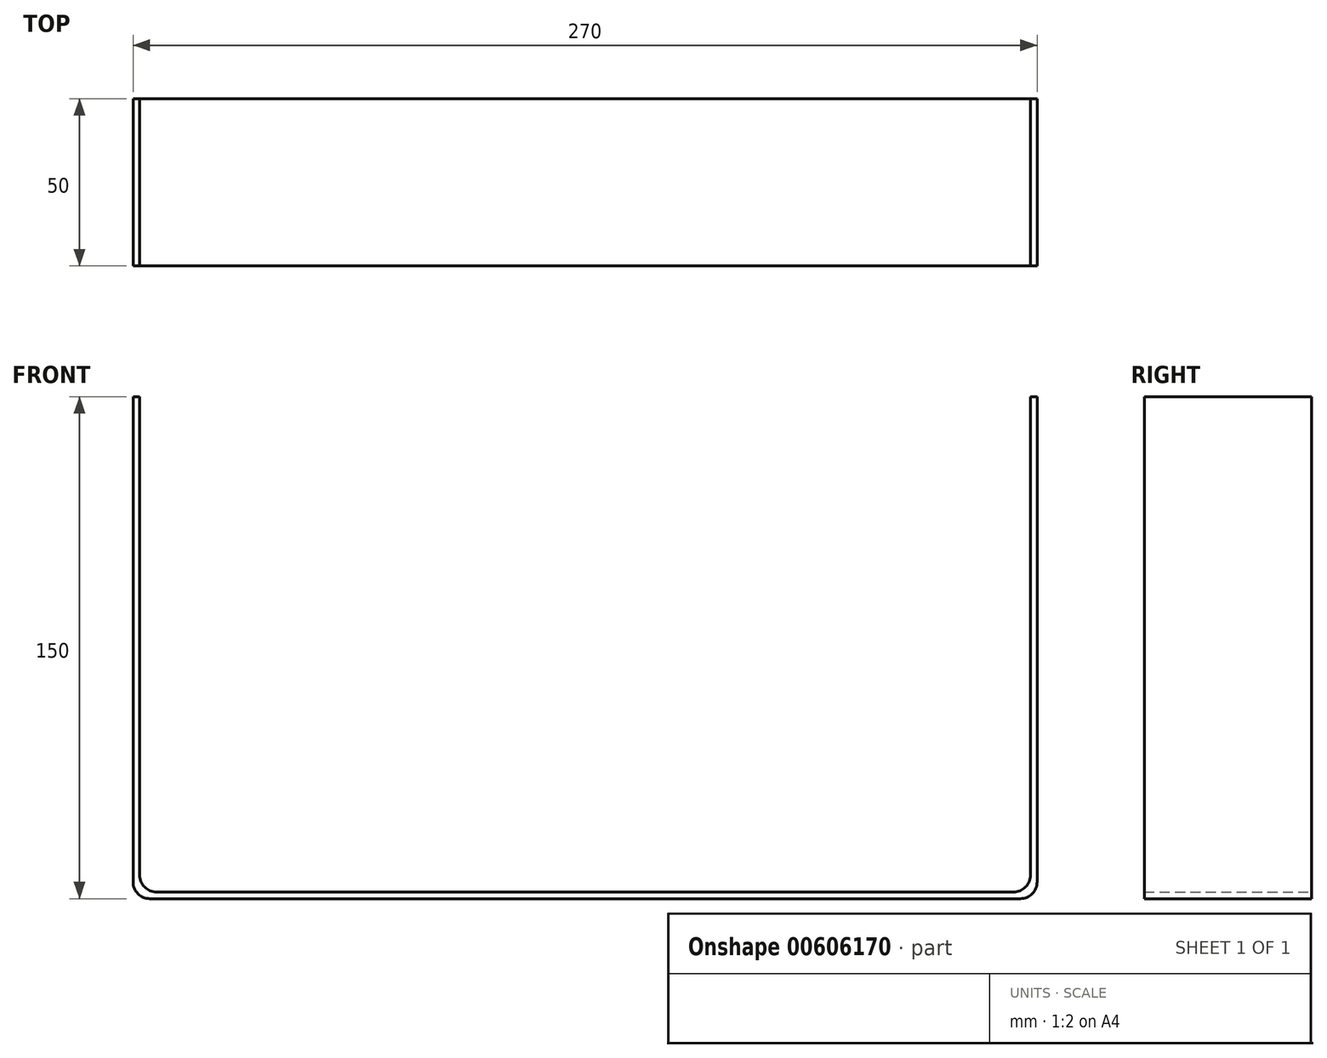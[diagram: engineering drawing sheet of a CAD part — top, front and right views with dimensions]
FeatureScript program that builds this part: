
annotation { "Feature Type Name" : "Feature", "Feature Type Description" : "" }
export const myFeature = defineFeature(function(context is Context, id is Id, definition is map)
    precondition{}
    {
        {
            var Q0;
            Q0=qCreatedBy(makeId("Front.planeOp"),FACE);
            var sketch = newSketch(context, id + "F0", { "sketchPlane" : qUnion([Q0])});
            skLineSegment(sketch, "E0.top", {"start": v(2, 2) * mm, "end": v(268, 2) * mm});
            skLineSegment(sketch, "E1.top", {"start": v(0, 150) * mm, "end": v(2, 150) * mm});
            skLineSegment(sketch, "E1.right", {"start": v(2, 2) * mm, "end": v(2, 150) * mm});
            skLineSegment(sketch, "E2.top", {"start": v(270, 150) * mm, "end": v(268, 150) * mm});
            skLineSegment(sketch, "E2.right", {"start": v(268, 2) * mm, "end": v(268, 150) * mm});
            skPoint(sketch, "E0.left.start.orphan", {"position": v(0, 0) * mm});
            skLineSegment(sketch, "E3", {"start": v(0, 150) * mm, "end": v(0, 0) * mm});
            skPoint(sketch, "E2.bottom.start.orphan", {"position": v(270, 0) * mm});
            skLineSegment(sketch, "E4", {"start": v(270, 150) * mm, "end": v(270, 0) * mm});
            skLineSegment(sketch, "E5", {"start": v(0, 0) * mm, "end": v(270, 0) * mm});
            skSolve(sketch);
        }
        {
            var Q0;
            Q0 = qSketchRegion(id + "F0", true);
            extrude(context, id + "F1", {"entities" : qUnion([Q0]), "depth" : 50 * mm, "offsetDistance" : 25 * mm});
        }
        {
            var Q0;
            Q0 = qSketchRegion(id + "F0", true);
            extrude(context, id + "F2", {"entities" : qUnion([Q0]), "operationType" : NewBodyOperationType.ADD, "depth" : 25 * mm, "offsetDistance" : 25 * mm});
        }
        {
            var Q0;
            Q0=makeQuery(id+"F1.opExtrude","SWEPT_EDGE",EDGE,{"disambiguationData":[OSD([sQuery(id+"F0.wireOp",EDGE,"E3"),sQuery(id+"F0.wireOp",EDGE,"E5")])]});
            fillet(context, id + "F3", {"entities" : qUnion([Q0]), "radius" : 5 * mm, "tangentPropagation" : true, "allowEdgeOverflow" : false});
        }
        {
            var Q0;
            Q0=makeQuery(id+"F1.opExtrude","SWEPT_EDGE",EDGE,{"disambiguationData":[OSD([sQuery(id+"F0.wireOp",EDGE,"E0.top"),sQuery(id+"F0.wireOp",EDGE,"E1.right")])]});
            fillet(context, id + "F4", {"entities" : qUnion([Q0]), "radius" : 5 * mm, "tangentPropagation" : true, "allowEdgeOverflow" : false});
        }
        {
            var Q0;
            Q0=makeQuery(id+"F1.opExtrude","SWEPT_EDGE",EDGE,{"disambiguationData":[OSD([sQuery(id+"F0.wireOp",EDGE,"E4"),sQuery(id+"F0.wireOp",EDGE,"E5")])]});
            fillet(context, id + "F5", {"entities" : qUnion([Q0]), "radius" : 5 * mm, "tangentPropagation" : true, "allowEdgeOverflow" : false});
        }
        {
            var Q0;
            Q0=makeQuery(id+"F1.opExtrude","SWEPT_EDGE",EDGE,{"disambiguationData":[OSD([sQuery(id+"F0.wireOp",EDGE,"E0.top"),sQuery(id+"F0.wireOp",EDGE,"E2.right")])]});
            fillet(context, id + "F6", {"entities" : qUnion([Q0]), "radius" : 5 * mm, "tangentPropagation" : true, "allowEdgeOverflow" : false});
        }
    });
